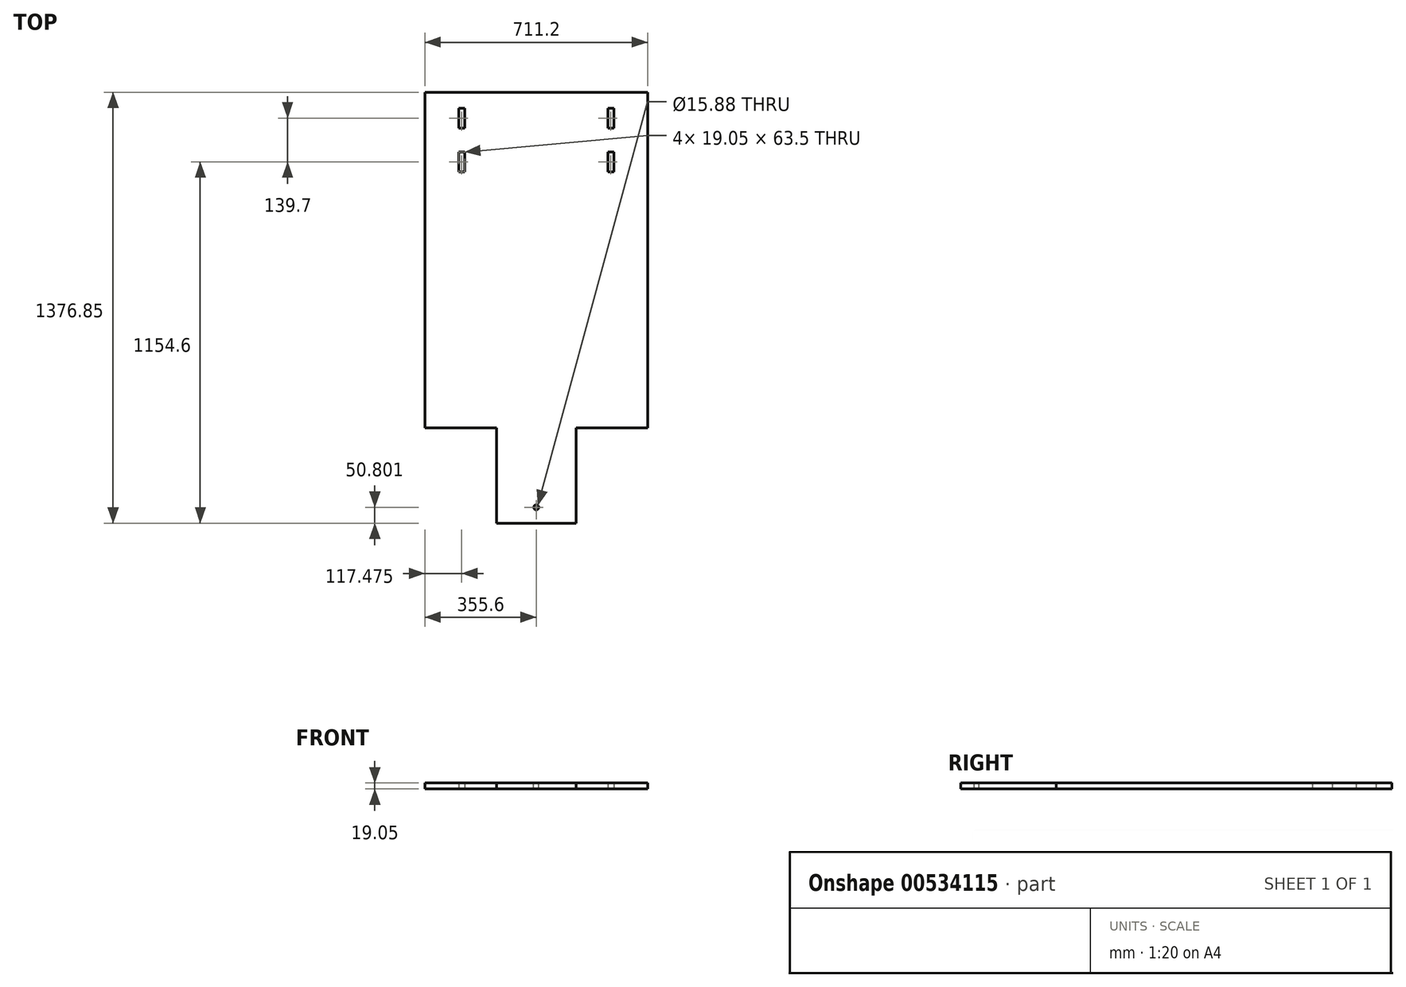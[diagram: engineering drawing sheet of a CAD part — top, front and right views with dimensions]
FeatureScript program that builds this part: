
annotation { "Feature Type Name" : "Feature", "Feature Type Description" : "" }
export const myFeature = defineFeature(function(context is Context, id is Id, definition is map)
    precondition{}
    {
        {
            var Q0;
            Q0=qCreatedBy(makeId("Top.planeOp"),FACE);
            var sketch = newSketch(context, id + "F0", { "sketchPlane" : qUnion([Q0])});
            skLineSegment(sketch, "E0", {"start": v(711.2, 304.8) * mm, "end": v(711.2, 1371.6) * mm, "construction": true});
            skLineSegment(sketch, "E1", {"start": v(203.2, 304.8) * mm, "end": v(203.2, 1371.6) * mm, "construction": true});
            skLineSegment(sketch, "E2", {"start": v(635, 1371.6) * mm, "end": v(635, 1320.8) * mm, "construction": true});
            skLineSegment(sketch, "E3", {"start": v(635, 1320.8) * mm, "end": v(635, 1257.3) * mm});
            skLineSegment(sketch, "E4", {"start": v(635, 1257.3) * mm, "end": v(635, 1181.1) * mm, "construction": true});
            skLineSegment(sketch, "E5", {"start": v(635, 1181.1) * mm, "end": v(635, 1117.6) * mm});
            skLineSegment(sketch, "E6", {"start": v(406.4, 0) * mm, "end": v(406.4, 1371.6) * mm, "construction": true});
            skLineSegment(sketch, "E7.MirrorCS", {"start": v(177.8, 1181.1) * mm, "end": v(177.8, 1117.6) * mm});
            skLineSegment(sketch, "E8.MirrorCS", {"start": v(177.8, 1320.8) * mm, "end": v(177.8, 1257.3) * mm});
            skLineSegment(sketch, "E9", {"start": v(635, 1181.1) * mm, "end": v(654.05, 1181.1) * mm});
            skLineSegment(sketch, "E10", {"start": v(654.05, 1181.1) * mm, "end": v(654.05, 1117.6) * mm});
            skLineSegment(sketch, "E11", {"start": v(654.05, 1117.6) * mm, "end": v(635, 1117.6) * mm});
            skLineSegment(sketch, "E12.MirrorCS", {"start": v(158.75, 1117.6) * mm, "end": v(177.8, 1117.6) * mm});
            skLineSegment(sketch, "E13.MirrorCS", {"start": v(158.75, 1181.1) * mm, "end": v(158.75, 1117.6) * mm});
            skLineSegment(sketch, "E14.MirrorCS", {"start": v(177.8, 1181.1) * mm, "end": v(158.75, 1181.1) * mm});
            skLineSegment(sketch, "E15", {"start": v(635, 1257.3) * mm, "end": v(654.05, 1257.3) * mm});
            skLineSegment(sketch, "E16", {"start": v(654.05, 1257.3) * mm, "end": v(654.05, 1320.8) * mm});
            skLineSegment(sketch, "E17", {"start": v(654.05, 1320.8) * mm, "end": v(635, 1320.8) * mm});
            skLineSegment(sketch, "E18.MirrorCS", {"start": v(177.8, 1257.3) * mm, "end": v(158.75, 1257.3) * mm});
            skLineSegment(sketch, "E19.MirrorCS", {"start": v(158.75, 1257.3) * mm, "end": v(158.75, 1320.8) * mm});
            skLineSegment(sketch, "E20.MirrorCS", {"start": v(158.75, 1320.8) * mm, "end": v(177.8, 1320.8) * mm});
            skLineSegment(sketch, "E21", {"start": v(50.8, 1371.6) * mm, "end": v(50.8, 299.55) * mm});
            skLineSegment(sketch, "E22", {"start": v(762, 299.55) * mm, "end": v(762, 1371.6) * mm});
            skPoint(sketch, "E23.middle", {"position": v(406.4, 372.6) * mm});
            skLineSegment(sketch, "E24", {"start": v(533.4, 299.55) * mm, "end": v(533.4, -5.25) * mm});
            skLineSegment(sketch, "E25", {"start": v(533.4, -5.25) * mm, "end": v(279.4, -5.25) * mm});
            skLineSegment(sketch, "E26", {"start": v(279.4, -5.25) * mm, "end": v(279.4, 299.55) * mm});
            skLineSegment(sketch, "E27", {"start": v(279.4, 299.55) * mm, "end": v(50.8, 299.55) * mm});
            skLineSegment(sketch, "E28", {"start": v(279.4, 299.55) * mm, "end": v(279.4, 197.95) * mm});
            skLineSegment(sketch, "E29", {"start": v(279.4, 197.95) * mm, "end": v(533.4, 197.95) * mm, "construction": true});
            skLineSegment(sketch, "E30", {"start": v(533.4, 197.95) * mm, "end": v(533.4, 299.55) * mm});
            skLineSegment(sketch, "E31", {"start": v(50.8, 1371.6) * mm, "end": v(762, 1371.6) * mm});
            skLineSegment(sketch, "E32", {"start": v(50.8, 299.55) * mm, "end": v(279.4, 299.55) * mm});
            skLineSegment(sketch, "E33", {"start": v(762, 299.55) * mm, "end": v(533.4, 299.55) * mm});
            skSolve(sketch);
        }
        {
            var Q0;
            Q0=makeQuery(id+"F0.imprint","IMPRINT",FACE,{"disambiguationData":[TD([[makeQuery(id+"F0.imprint","IMPRINT",EDGE,{"derivedFrom":sQuery(id+"F0.wireOp",EDGE,"E3")}),-1.0]])]});
            extrude(context, id + "F1", {"entities" : qUnion([Q0]), "depth" : 19.05 * mm, "offsetDistance" : 25.4 * mm});
        }
        {
            var Q0;
            Q0=makeQuery(id+"F1.opExtrude","CAP_FACE",FACE,{"disambiguationData":[OSD([sQuery(id+"F0.wireOp",EDGE,"E3"),sQuery(id+"F0.wireOp",EDGE,"E5"),sQuery(id+"F0.wireOp",EDGE,"E7.MirrorCS"),sQuery(id+"F0.wireOp",EDGE,"E8.MirrorCS"),sQuery(id+"F0.wireOp",EDGE,"E9"),sQuery(id+"F0.wireOp",EDGE,"E10"),sQuery(id+"F0.wireOp",EDGE,"E11"),sQuery(id+"F0.wireOp",EDGE,"E12.MirrorCS"),sQuery(id+"F0.wireOp",EDGE,"E13.MirrorCS"),sQuery(id+"F0.wireOp",EDGE,"E14.MirrorCS"),sQuery(id+"F0.wireOp",EDGE,"E15"),sQuery(id+"F0.wireOp",EDGE,"E16"),sQuery(id+"F0.wireOp",EDGE,"E17"),sQuery(id+"F0.wireOp",EDGE,"E18.MirrorCS"),sQuery(id+"F0.wireOp",EDGE,"E19.MirrorCS"),sQuery(id+"F0.wireOp",EDGE,"E20.MirrorCS"),sQuery(id+"F0.wireOp",EDGE,"4b0ce99d-92c2-4d5a-877c-9357c4aba25a0.MirrorCS"),sQuery(id+"F0.wireOp",EDGE,"E21"),sQuery(id+"F0.wireOp",EDGE,"E22"),sQuery(id+"F0.wireOp",EDGE,"VkGcMUjl-mB8C-SwPy-fy5Y-xW25E71paEz6"),sQuery(id+"F0.wireOp",EDGE,"E24"),sQuery(id+"F0.wireOp",EDGE,"E25"),sQuery(id+"F0.wireOp",EDGE,"E26"),sQuery(id+"F0.wireOp",EDGE,"E27"),sQuery(id+"F0.wireOp",EDGE,"E28"),sQuery(id+"F0.wireOp",EDGE,"E30")])],"isStart":false});
            var sketch = newSketch(context, id + "F2", { "sketchPlane" : qUnion([Q0])});
            skCircle(sketch, "E34", {"center": v(406.4, 45.55) * mm, "radius": 7.94 * mm});
            skLineSegment(sketch, "E35", {"start": v(406.4, -5.25) * mm, "end": v(406.4, 308.97) * mm, "construction": true});
            skLineSegment(sketch, "E36", {"start": v(279.4, 45.55) * mm, "end": v(533.4, 45.55) * mm, "construction": true});
            skSolve(sketch);
        }
        {
            var Q0;
            Q0=makeQuery(id+"F2.imprint","IMPRINT",FACE,{"disambiguationData":[TD([[makeQuery(id+"F2.imprint","IMPRINT",EDGE,{"derivedFrom":sQuery(id+"F2.wireOp",EDGE,"E34")}),1.0]])]});
            extrude(context, id + "F3", {"entities" : qUnion([Q0]), "operationType" : NewBodyOperationType.REMOVE, "endBound" : BoundingType.UP_TO_NEXT, "oppositeDirection" : true, "depth" : 25.4 * mm, "offsetDistance" : 25.4 * mm});
        }
    });
